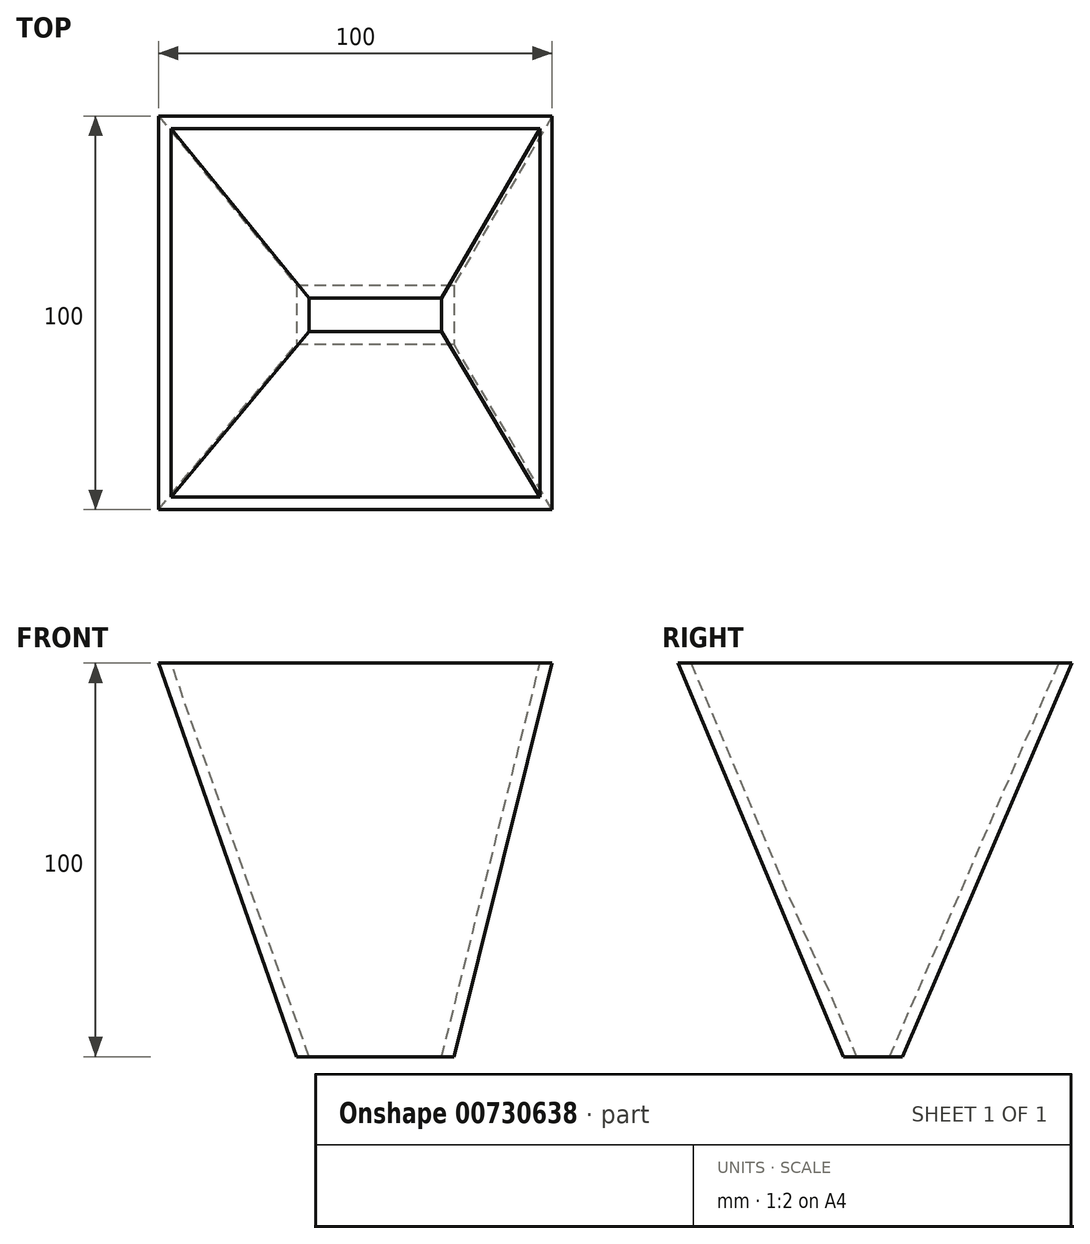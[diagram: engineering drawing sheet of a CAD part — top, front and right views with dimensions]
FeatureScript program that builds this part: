
annotation { "Feature Type Name" : "Feature", "Feature Type Description" : "" }
export const myFeature = defineFeature(function(context is Context, id is Id, definition is map)
    precondition{}
    {
        {
            var Q0;
            Q0=qCreatedBy(makeId("Top.planeOp"),FACE);
            cPlane(context, id + "F0", {"entities" : qUnion([Q0]), "cplaneType" : CPlaneType.OFFSET, "offset" : 100 * mm, "width" : 150 * mm, "height" : 150 * mm});
        }
        {
            var Q0;
            Q0=qCreatedBy(id+"F0.planeOp",FACE);
            var sketch = newSketch(context, id + "F1", { "sketchPlane" : qUnion([Q0])});
            skLineSegment(sketch, "E0.bottom", {"start": v(0, 0) * mm, "end": v(100, 0) * mm});
            skLineSegment(sketch, "E0.top", {"start": v(0, -100) * mm, "end": v(100, -100) * mm});
            skLineSegment(sketch, "E0.left", {"start": v(0, 0) * mm, "end": v(0, -100) * mm});
            skLineSegment(sketch, "E0.right", {"start": v(100, 0) * mm, "end": v(100, -100) * mm});
            skSolve(sketch);
        }
        {
            var Q0;
            Q0=qCreatedBy(makeId("Top.planeOp"),FACE);
            var sketch = newSketch(context, id + "F2", { "sketchPlane" : qUnion([Q0])});
            skLineSegment(sketch, "E1.bottom", {"start": v(35, -43) * mm, "end": v(75, -43) * mm});
            skLineSegment(sketch, "E1.top", {"start": v(35, -58) * mm, "end": v(75, -58) * mm});
            skLineSegment(sketch, "E1.left", {"start": v(35, -43) * mm, "end": v(35, -58) * mm});
            skLineSegment(sketch, "E1.right", {"start": v(75, -43) * mm, "end": v(75, -58) * mm});
            skSolve(sketch);
        }
        {
            var Q0;
            Q0=makeQuery(id+"F1.imprint","IMPRINT",FACE,{"disambiguationData":[TD([[makeQuery(id+"F1.imprint","IMPRINT",EDGE,{"derivedFrom":sQuery(id+"F1.wireOp",EDGE,"E0.bottom")}),-1.0]])]});
            var Q1;
            Q1=makeQuery(id+"F2.imprint","IMPRINT",FACE,{"disambiguationData":[TD([[makeQuery(id+"F2.imprint","IMPRINT",EDGE,{"derivedFrom":sQuery(id+"F2.wireOp",EDGE,"E1.bottom")}),-1.0]])]});
            loft(context, id + "F3", {"sheetProfilesArray" : [{ "sheetProfileEntities" : qUnion([Q0]) }, { "sheetProfileEntities" : qUnion([Q1]) }]});
        }
        {
            var Q0;
            Q0=makeQuery(id+"F3.opLoft","CAP_FACE",FACE,{"disambiguationData":[OSD([makeQuery(id+"F1.imprint","IMPRINT",FACE,{"disambiguationData":[TD([[makeQuery(id+"F1.imprint","IMPRINT",EDGE,{"derivedFrom":sQuery(id+"F1.wireOp",EDGE,"E0.bottom")}),-1.0]])]})])],"isStart":true});
            var Q1;
            Q1=makeQuery(id+"F3.opLoft","CAP_FACE",FACE,{"disambiguationData":[OSD([makeQuery(id+"F2.imprint","IMPRINT",FACE,{"disambiguationData":[TD([[makeQuery(id+"F2.imprint","IMPRINT",EDGE,{"derivedFrom":sQuery(id+"F2.wireOp",EDGE,"E1.bottom")}),-1.0]])]})])],"isStart":true});
            shell(context, id + "F4", {"entities" : qUnion([Q0, Q1]), "thickness" : 3 * mm});
        }
    });
